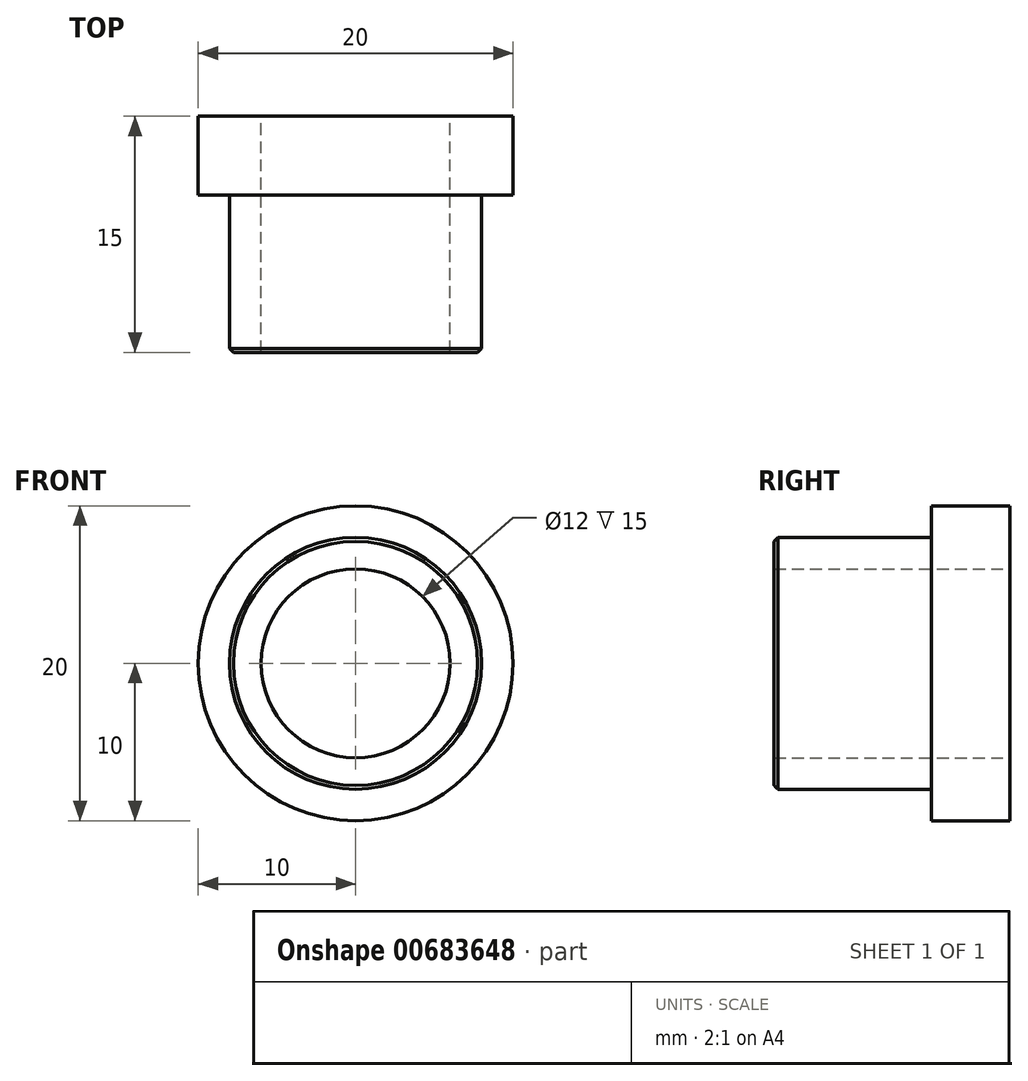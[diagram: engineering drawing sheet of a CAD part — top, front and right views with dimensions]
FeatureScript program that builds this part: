
annotation { "Feature Type Name" : "Feature", "Feature Type Description" : "" }
export const myFeature = defineFeature(function(context is Context, id is Id, definition is map)
    precondition{}
    {
        {
            var Q0;
            Q0=qCreatedBy(makeId("Front.planeOp"),FACE);
            var sketch = newSketch(context, id + "F0", { "sketchPlane" : qUnion([Q0])});
            skCircle(sketch, "E0", {"center": v(0, 0) * mm, "radius": 10 * mm});
            skCircle(sketch, "E1", {"center": v(0, 0) * mm, "radius": 8 * mm});
            skCircle(sketch, "E2", {"center": v(0, 0) * mm, "radius": 6 * mm});
            skSolve(sketch);
        }
        {
            var Q0;
            Q0=makeQuery(id+"F0.imprint","IMPRINT",FACE,{"disambiguationData":[TD([[makeQuery(id+"F0.imprint","IMPRINT",EDGE,{"derivedFrom":sQuery(id+"F0.wireOp",EDGE,"E1")}),1.0]])]});
            extrude(context, id + "F1", {"entities" : qUnion([Q0]), "depth" : 15 * mm, "offsetDistance" : 25 * mm});
        }
        {
            var Q0;
            Q0 = qSketchRegion(id + "F0", true);
            extrude(context, id + "F2", {"entities" : qUnion([Q0]), "operationType" : NewBodyOperationType.ADD, "depth" : 5 * mm, "offsetDistance" : 25 * mm});
        }
        {
            var Q0;
            Q0=makeQuery(id+"F1.opExtrude","CAP_EDGE",EDGE,{"disambiguationData":[OSD([sQuery(id+"F0.wireOp",EDGE,"E1")])],"isStart":false});
            chamfer(context, id + "F3", {"entities" : qUnion([Q0]), "width" : .25 * mm, "tangentPropagation" : true});
        }
    });
